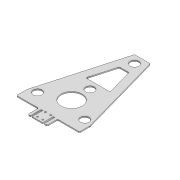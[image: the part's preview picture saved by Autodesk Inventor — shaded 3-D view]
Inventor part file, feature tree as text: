
AUTODESK INVENTOR PART (.ipt)
format: ipt  version: 2022 (Build 260153000, 153)  size: 287,744 bytes
history: native  units: mm
features: extrude x4, sketch x4, projected_geometry x3, fillet x1
ambient origin geometry x8: Origin, YZ Plane, XZ Plane, XY Plane, X Axis, Y Axis, Z Axis, Center Point
bodies: Solid1 (feature_tree)
feature tree (12):
  extrude  "Extrusion1"  Depth=20.0mm
  fillet  "Fillet1"  Radius=120.0mm
  sketch  "Sketch6"  dims[d3=60.0mm d4=20.0mm]
  sketch  "Sketch7"  dims[d6=200.0mm d7=45.0mm]
  extrude  "Extrusion3"  Depth=20.0mm
  extrude  "Extrusion4"  Depth=200.0mm
  extrude  "Extrusion5"  Depth=5.0mm
  sketch  "Sketch1"  dims[d0=20.0mm d1=20.0mm d2=120.0mm]
  projected_geometry  "Projected Loop4"
  projected_geometry  "Projected Loop5"
  sketch  "Sketch8"  dims[d8=45.0mm d9=16.5mm d10=16.5mm d11=16.5mm d12=16.5mm d13=15.0mm d14=15.0mm d15=25.0mm d16=25.0mm d17=15.0mm d18=100.0mm d23=3.0mm d24=3.0mm d25=3.0mm d26=3.0mm d27=5.0mm d28=5.0mm d29=5.0mm d30=5.0mm d31=0.0mm d32=0.0mm d33=5.0mm d34=5.0mm d35=2.0mm d36=0.0mm d37=2.0mm d38=3.1mm d39=3.1mm d40=5.0mm d41=5.0mm d56=15.0mm d57=15.0mm d58=20.0mm d59=15.0mm d64=40.0mm d66=35.0mm d67=16.2mm d68=16.2mm d69=16.2mm d70=16.2mm d71=3.0mm d72=3.0mm d73=3.0mm d74=3.0mm d75=5.0mm d76=0.0mm d77=30.0mm d78=0.0mm d79=0.1mm d80=0.1mm d81=0.1mm d82=0.1mm d83=30.0mm d84=0.0mm]
  projected_geometry  "Projected Loop6"
